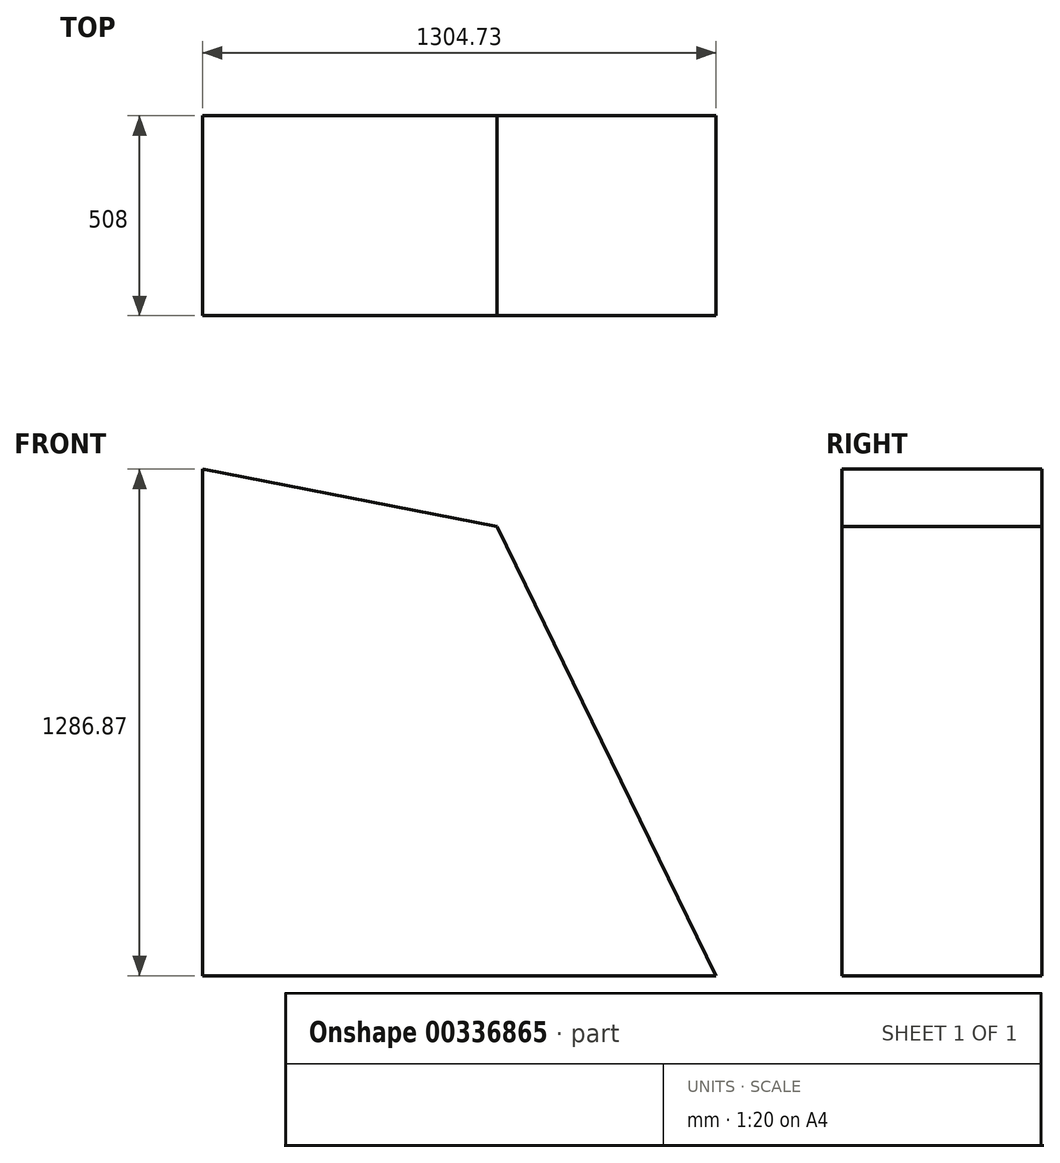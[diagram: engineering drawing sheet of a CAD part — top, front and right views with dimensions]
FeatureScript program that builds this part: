
annotation { "Feature Type Name" : "Feature", "Feature Type Description" : "" }
export const myFeature = defineFeature(function(context is Context, id is Id, definition is map)
    precondition{}
    {
        {
            var Q0;
            Q0=qCreatedBy(makeId("Front.planeOp"),FACE);
            var sketch = newSketch(context, id + "F0", { "sketchPlane" : qUnion([Q0])});
            skLineSegment(sketch, "E0", {"start": v(-921.71, 885.98) * mm, "end": v(-173.71, 740.58) * mm});
            skLineSegment(sketch, "E1", {"start": v(-173.71, 740.58) * mm, "end": v(383.02, -400.89) * mm});
            skLineSegment(sketch, "E2", {"start": v(383.02, -400.89) * mm, "end": v(-921.71, -400.89) * mm});
            skLineSegment(sketch, "E3", {"start": v(-921.71, -400.89) * mm, "end": v(-921.71, 885.98) * mm});
            skSolve(sketch);
        }
        {
            var Q0;
            Q0=makeQuery(id+"F0.imprint","IMPRINT",FACE,{"disambiguationData":[TD([[makeQuery(id+"F0.imprint","IMPRINT",EDGE,{"derivedFrom":sQuery(id+"F0.wireOp",EDGE,"E0")}),-1.0]])]});
            extrude(context, id + "F1", {"entities" : qUnion([Q0]), "depth" : 508 * mm});
        }
    });
